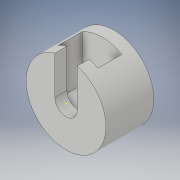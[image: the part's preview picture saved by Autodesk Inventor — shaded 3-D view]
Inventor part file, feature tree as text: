
AUTODESK INVENTOR PART (.ipt)
format: ipt  version: 2019 (Build 230136000, 136)  size: 131,584 bytes
history: native  units: mm
features: sketch x7, extrude x4, plane x1, hole x1, projected_geometry x1
ambient origin geometry x8: Origin, YZ Plane, XZ Plane, XY Plane, X Axis, Y Axis, Z Axis, Center Point
bodies: Solid1 (feature_tree)
feature tree (14):
  sketch  "Sketch1"  dims[d0=25.0mm d1=15.0mm d2=0.0mm]
  extrude  "Extrusion1"  Depth=15.0mm TaperAngle=0.0deg
  plane  "Work Plane1"
  extrude  "Extrusion2"  Depth=12.4mm
  extrude  "Extrusion3"  Depth=15.0mm TaperAngle=0.0deg
  hole  "Hole1"  [1 undecoded]
  sketch  "Sketch6"
  extrude  "Extrusion4"  [1 undecoded]
  sketch  "Sketch2"  dims[d3=7.5mm d4=12.4mm]
  sketch  "Sketch3"  dims[d5=7.5mm d6=0.0mm d7=15.0mm d8=0.0mm]
  sketch  "Sketch4"  dims[d9=7.0mm d10=6.0mm d11=5.0mm d12=3.0mm d13=90.0deg d14=7.5mm d15=0.0mm d16=15.0mm d17=0.0mm]
  sketch  "Sketch5"
  sketch  "Sketch7"
  projected_geometry  "Projected Loop1"
note: 2 required parameter values undecoded (feature->parameter linkage not recoverable at this tier; creation-order binding heuristic only, values carry confidence <= 0.55)
